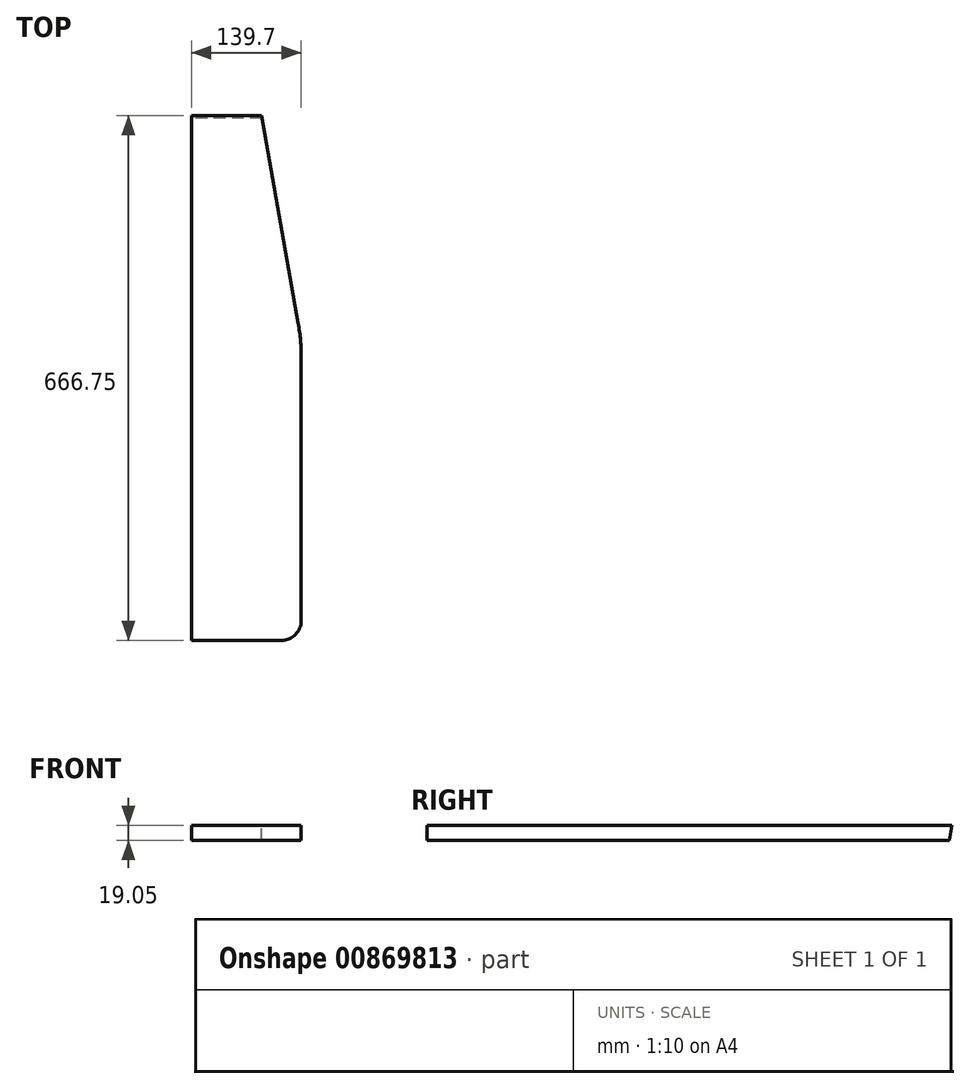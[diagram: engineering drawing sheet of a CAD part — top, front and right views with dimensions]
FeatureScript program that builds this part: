
annotation { "Feature Type Name" : "Feature", "Feature Type Description" : "" }
export const myFeature = defineFeature(function(context is Context, id is Id, definition is map)
    precondition{}
    {
        {
            var Q0;
            Q0=qCreatedBy(makeId("Top.planeOp"),FACE);
            var sketch = newSketch(context, id + "F0", { "sketchPlane" : qUnion([Q0])});
            skLineSegment(sketch, "E0", {"start": v(0, 0) * mm, "end": v(139.7, 0) * mm});
            skLineSegment(sketch, "E1", {"start": v(139.7, 0) * mm, "end": v(139.7, 381) * mm});
            skLineSegment(sketch, "E2", {"start": v(88.9, 666.75) * mm, "end": v(0, 666.75) * mm});
            skLineSegment(sketch, "E3", {"start": v(0, 666.75) * mm, "end": v(0, 0) * mm});
            skLineSegment(sketch, "E4", {"start": v(88.9, 666.75) * mm, "end": v(139.7, 381) * mm});
            skSolve(sketch);
        }
        {
            var Q0;
            Q0 = qSketchRegion(id + "F0", true);
            extrude(context, id + "F1", {"entities" : qUnion([Q0]), "depth" : 19.05 * mm, "offsetDistance" : 25.4 * mm});
        }
        {
            var Q0;
            Q0=makeQuery(id+"F1.opExtrude","SWEPT_EDGE",EDGE,{"disambiguationData":[OSD([sQuery(id+"F0.wireOp",EDGE,"E1"),sQuery(id+"F0.wireOp",EDGE,"E4")])]});
            fillet(context, id + "F2", {"entities" : qUnion([Q0]), "radius" : 254 * mm, "tangentPropagation" : true, "allowEdgeOverflow" : false});
        }
        {
            var Q0;
            Q0=makeQuery(id+"F1.opExtrude","SWEPT_EDGE",EDGE,{"disambiguationData":[OSD([sQuery(id+"F0.wireOp",EDGE,"E0"),sQuery(id+"F0.wireOp",EDGE,"E1")])]});
            fillet(context, id + "F3", {"entities" : qUnion([Q0]), "radius" : 25.4 * mm, "tangentPropagation" : true, "allowEdgeOverflow" : false});
        }
        {
            var Q0;
            Q0=makeQuery(id+"F1.opExtrude","SWEPT_FACE",FACE,{"disambiguationData":[OSD([sQuery(id+"F0.wireOp",EDGE,"E3")])]});
            var sketch = newSketch(context, id + "F4", { "sketchPlane" : qUnion([Q0])});
            skLineSegment(sketch, "E5", {"start": v(-666.75, 19.05) * mm, "end": v(-663.4, 0) * mm});
            skLineSegment(sketch, "E6", {"start": v(-663.4, 0) * mm, "end": v(-666.75, 0) * mm});
            skLineSegment(sketch, "E7", {"start": v(-666.75, 0) * mm, "end": v(-666.75, 19.05) * mm});
            skSolve(sketch);
        }
        {
            var Q0;
            Q0 = qSketchRegion(id + "F4", true);
            extrude(context, id + "F5", {"entities" : qUnion([Q0]), "operationType" : NewBodyOperationType.REMOVE, "endBound" : BoundingType.THROUGH_ALL, "oppositeDirection" : true, "depth" : 25.4 * mm, "offsetDistance" : 25.4 * mm});
        }
    });
